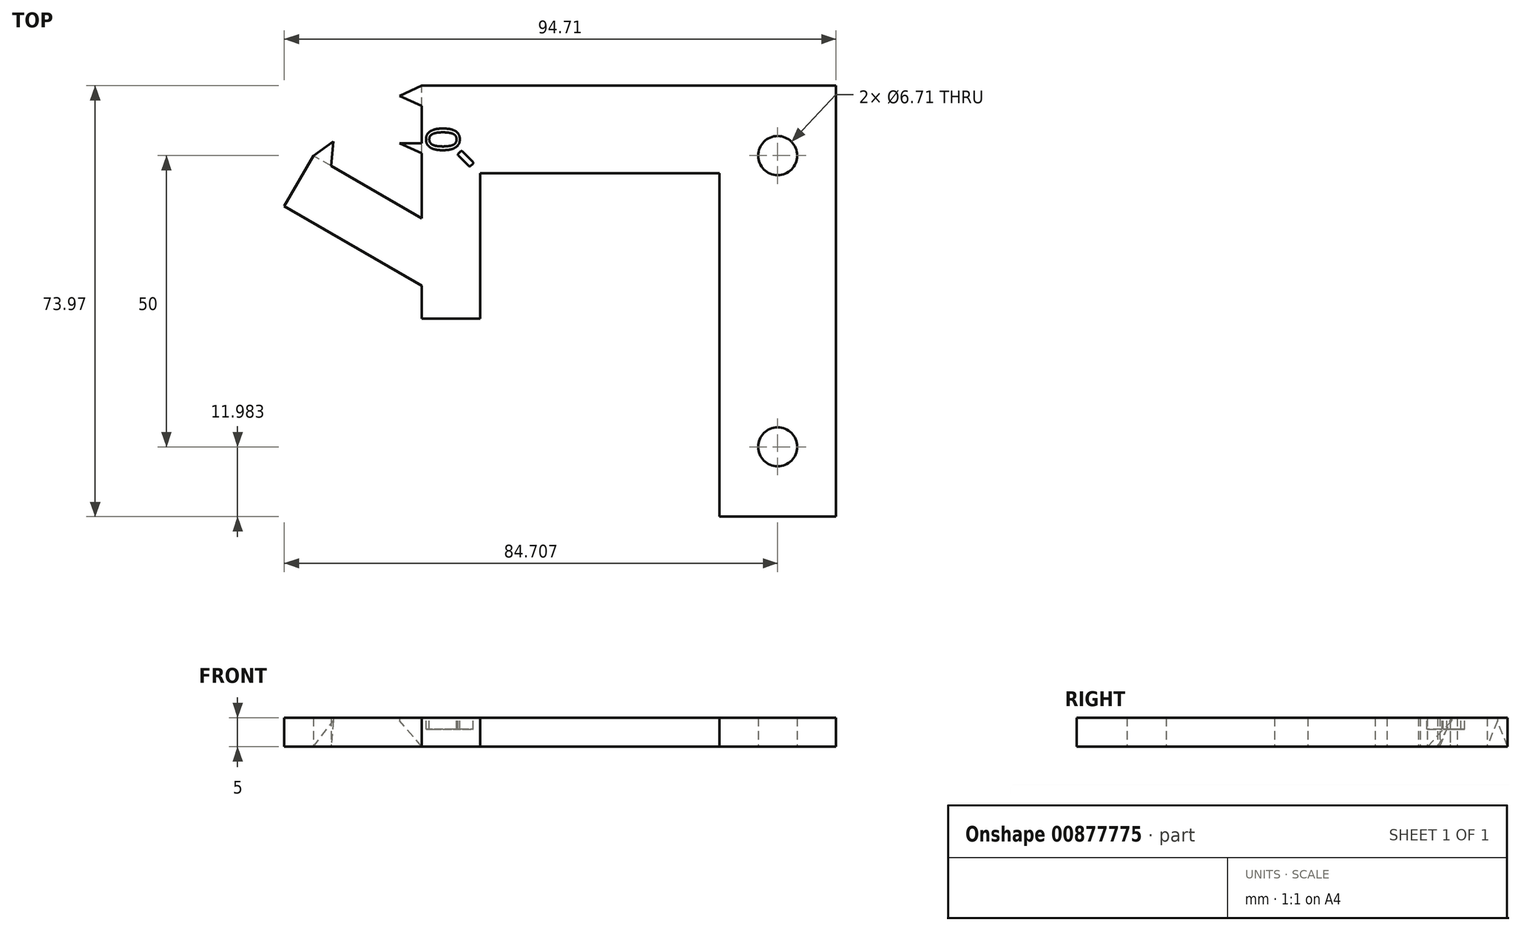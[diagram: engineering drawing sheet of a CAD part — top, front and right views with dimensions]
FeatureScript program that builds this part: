
annotation { "Feature Type Name" : "Feature", "Feature Type Description" : "" }
export const myFeature = defineFeature(function(context is Context, id is Id, definition is map)
    precondition{}
    {
        {
            var Q0;
            Q0=qCreatedBy(makeId("Top.planeOp"),FACE);
            var sketch = newSketch(context, id + "F0", { "sketchPlane" : qUnion([Q0])});
            skLineSegment(sketch, "E0.bottom", {"start": v(11.28, 11.46) * mm, "end": v(21.28, 11.46) * mm});
            skLineSegment(sketch, "E0.top", {"start": v(11.28, 51.46) * mm, "end": v(21.28, 51.46) * mm});
            skLineSegment(sketch, "E0.left", {"start": v(11.28, 11.46) * mm, "end": v(11.28, 51.46) * mm});
            skLineSegment(sketch, "E0.right", {"start": v(21.28, 11.46) * mm, "end": v(21.28, 51.46) * mm});
            skPoint(sketch, "E1.0.midPoint", {"position": v(11.28, 51.46) * mm});
            skLineSegment(sketch, "E2", {"start": v(11.28, 51.46) * mm, "end": v(7.47, 49.71) * mm});
            skLineSegment(sketch, "E3", {"start": v(7.47, 49.71) * mm, "end": v(11.28, 47.97) * mm});
            skLineSegment(sketch, "E4", {"start": v(7.47, 49.71) * mm, "end": v(11.28, 49.71) * mm});
            skLineSegment(sketch, "E5", {"start": v(11.28, 39.84) * mm, "end": v(7.47, 41.58) * mm});
            skLineSegment(sketch, "E6", {"start": v(7.47, 41.58) * mm, "end": v(11.28, 41.58) * mm});
            skLineSegment(sketch, "E7", {"start": v(11.28, 41.58) * mm, "end": v(7.47, 41.58) * mm});
            skLineSegment(sketch, "E8", {"start": v(7.47, 41.58) * mm, "end": v(11.28, 43.33) * mm});
            skLineSegment(sketch, "E9.bottom", {"start": v(-7.32, 39.44) * mm, "end": v(21.28, 22.93) * mm});
            skLineSegment(sketch, "E9.top", {"start": v(-12.32, 30.78) * mm, "end": v(16.28, 14.27) * mm});
            skLineSegment(sketch, "E9.left", {"start": v(-7.32, 39.44) * mm, "end": v(-12.32, 30.78) * mm});
            skLineSegment(sketch, "E9.right", {"start": v(21.28, 22.93) * mm, "end": v(16.28, 14.27) * mm});
            skLineSegment(sketch, "E10", {"start": v(-4.3, 37.7) * mm, "end": v(-3.9, 41.87) * mm});
            skLineSegment(sketch, "E11", {"start": v(-3.9, 41.87) * mm, "end": v(-7.32, 39.44) * mm});
            skLineSegment(sketch, "E12", {"start": v(-3.9, 41.87) * mm, "end": v(-5.81, 38.57) * mm});
            skLineSegment(sketch, "E13.bottom", {"start": v(62.39, -22.51) * mm, "end": v(82.39, -22.51) * mm});
            skLineSegment(sketch, "E13.top", {"start": v(62.39, 51.46) * mm, "end": v(82.39, 51.46) * mm});
            skLineSegment(sketch, "E13.left", {"start": v(62.39, -22.51) * mm, "end": v(62.39, 51.46) * mm});
            skLineSegment(sketch, "E13.right", {"start": v(82.39, -22.51) * mm, "end": v(82.39, 51.46) * mm});
            skCircle(sketch, "E14", {"center": v(72.39, -10.53) * mm, "radius": 3.35 * mm});
            skCircle(sketch, "E15", {"center": v(72.39, 39.47) * mm, "radius": 3.35 * mm});
            skLineSegment(sketch, "E16", {"start": v(72.39, 39.47) * mm, "end": v(72.39, -10.53) * mm});
            skLineSegment(sketch, "E17", {"start": v(72.39, -10.53) * mm, "end": v(72.39, -22.51) * mm});
            skLineSegment(sketch, "E18", {"start": v(72.39, 39.47) * mm, "end": v(72.39, 51.46) * mm});
            skLineSegment(sketch, "E19.bottom", {"start": v(62.39, 51.46) * mm, "end": v(21.28, 51.46) * mm});
            skLineSegment(sketch, "E19.top", {"start": v(62.39, 36.46) * mm, "end": v(21.28, 36.46) * mm});
            skLineSegment(sketch, "E19.left", {"start": v(62.39, 51.46) * mm, "end": v(62.39, 36.46) * mm});
            skLineSegment(sketch, "E19.right", {"start": v(21.28, 51.46) * mm, "end": v(21.28, 36.46) * mm});
            skLineSegment(sketch, "E20", {"start": v(62.39, 36.46) * mm, "end": v(62.39, 51.46) * mm});
            skLineSegment(sketch, "E21", {"start": v(21.28, 36.46) * mm, "end": v(21.28, 51.46) * mm});
            skSolve(sketch);
        }
        {
            var Q0;
            {var subQ6=sQuery(id+"F0.wireOp",EDGE,"47bd21e5-315e-477f-9ace-8077bcce72af.top");Q0=makeQuery(id+"F0.imprint","IMPRINT",FACE,{"disambiguationData":[TD([[makeQuery(id+"F0.imprint","IMPRINT",EDGE,{"derivedFrom":subQ6}),1.0]])]});}
            var Q1;
            {var subQ11=sQuery(id+"F0.wireOp",EDGE,"47bd21e5-315e-477f-9ace-8077bcce72af.bottom");Q1=makeQuery(id+"F0.imprint","IMPRINT",FACE,{"disambiguationData":[TD([[makeQuery(id+"F0.imprint","IMPRINT",EDGE,{"derivedFrom":subQ11}),-1.0]])]});}
            var Q2;
            {var subQ4=sQuery(id+"F0.wireOp",EDGE,"E0.bottom");Q2=makeQuery(id+"F0.imprint","IMPRINT",FACE,{"disambiguationData":[TD([[makeQuery(id+"F0.imprint","IMPRINT",EDGE,{"derivedFrom":subQ4}),1.0]])]});}
            var Q3;
            {var subQ5=sQuery(id+"F0.wireOp",EDGE,"E9.left");Q3=makeQuery(id+"F0.imprint","IMPRINT",FACE,{"disambiguationData":[TD([[makeQuery(id+"F0.imprint","IMPRINT",EDGE,{"derivedFrom":subQ5}),1.0]])]});}
            var Q4;
            {var subQ5=sQuery(id+"F0.wireOp",EDGE,"E9.right");Q4=makeQuery(id+"F0.imprint","IMPRINT",FACE,{"disambiguationData":[TD([[makeQuery(id+"F0.imprint","IMPRINT",EDGE,{"derivedFrom":subQ5}),-1.0]])]});}
            var Q5;
            {var subQ6=sQuery(id+"F0.wireOp",EDGE,"E0.top");Q5=makeQuery(id+"F0.imprint","IMPRINT",FACE,{"disambiguationData":[TD([[makeQuery(id+"F0.imprint","IMPRINT",EDGE,{"derivedFrom":subQ6}),-1.0]])]});}
            var Q6;
            {var subQ0=sQuery(id+"F0.wireOp",EDGE,"E5");Q6=makeQuery(id+"F0.imprint","IMPRINT",FACE,{"disambiguationData":[TD([[makeQuery(id+"F0.imprint","IMPRINT",EDGE,{"derivedFrom":subQ0}),-1.0]])]});}
            var Q7;
            {var subQ0=sQuery(id+"F0.wireOp",EDGE,"E7");Q7=makeQuery(id+"F0.imprint","IMPRINT",FACE,{"disambiguationData":[TD([[makeQuery(id+"F0.imprint","IMPRINT",EDGE,{"derivedFrom":subQ0}),-1.0]])]});}
            var Q8;
            {var subQ0=sQuery(id+"F0.wireOp",EDGE,"E3");Q8=makeQuery(id+"F0.imprint","IMPRINT",FACE,{"disambiguationData":[TD([[makeQuery(id+"F0.imprint","IMPRINT",EDGE,{"derivedFrom":subQ0}),1.0]])]});}
            var Q9;
            {var subQ0=sQuery(id+"F0.wireOp",EDGE,"E2");Q9=makeQuery(id+"F0.imprint","IMPRINT",FACE,{"disambiguationData":[TD([[makeQuery(id+"F0.imprint","IMPRINT",EDGE,{"derivedFrom":subQ0}),1.0]])]});}
            var Q10;
            {var subQ0=sQuery(id+"F0.wireOp",EDGE,"E10");Q10=makeQuery(id+"F0.imprint","IMPRINT",FACE,{"disambiguationData":[TD([[makeQuery(id+"F0.imprint","IMPRINT",EDGE,{"derivedFrom":subQ0}),1.0]])]});}
            var Q11;
            {var subQ0=sQuery(id+"F0.wireOp",EDGE,"E11");Q11=makeQuery(id+"F0.imprint","IMPRINT",FACE,{"disambiguationData":[TD([[makeQuery(id+"F0.imprint","IMPRINT",EDGE,{"derivedFrom":subQ0}),1.0]])]});}
            var Q12;
            Q12=makeQuery(id+"F0.imprint","IMPRINT",FACE,{"disambiguationData":[TD([[makeQuery(id+"F0.imprint","IMPRINT",EDGE,{"derivedFrom":sQuery(id+"F0.wireOp",EDGE,"E19.bottom")}),1.0]])]});
            var Q13;
            {var subQ5=sQuery(id+"F0.wireOp",EDGE,"E13.left");Q13=makeQuery(id+"F0.imprint","IMPRINT",FACE,{"disambiguationData":[TD([[makeQuery(id+"F0.imprint","IMPRINT",EDGE,{"derivedFrom":subQ5}),-1.0]])]});}
            var Q14;
            {var subQ5=sQuery(id+"F0.wireOp",EDGE,"E13.right");Q14=makeQuery(id+"F0.imprint","IMPRINT",FACE,{"disambiguationData":[TD([[makeQuery(id+"F0.imprint","IMPRINT",EDGE,{"derivedFrom":subQ5}),1.0]])]});}
            extrude(context, id + "F1", {"entities" : qUnion([Q0, Q1, Q2, Q3, Q4, Q5, Q6, Q7, Q8, Q9, Q10, Q11, Q12, Q13, Q14]), "depth" : 5 * mm, "offsetDistance" : 25 * mm});
        }
        {
            var Q0;
            Q0=makeQuery(id+"F1.opExtrude","CAP_FACE",FACE,{"disambiguationData":[OSD([sQuery(id+"F0.wireOp",EDGE,"E0.bottom"),sQuery(id+"F0.wireOp",EDGE,"E0.top"),sQuery(id+"F0.wireOp",EDGE,"E0.left"),sQuery(id+"F0.wireOp",EDGE,"E0.right"),sQuery(id+"F0.wireOp",EDGE,"E2"),sQuery(id+"F0.wireOp",EDGE,"E3"),sQuery(id+"F0.wireOp",EDGE,"E5"),sQuery(id+"F0.wireOp",EDGE,"E8"),sQuery(id+"F0.wireOp",EDGE,"E9.bottom"),sQuery(id+"F0.wireOp",EDGE,"E9.top"),sQuery(id+"F0.wireOp",EDGE,"E9.left"),sQuery(id+"F0.wireOp",EDGE,"E10"),sQuery(id+"F0.wireOp",EDGE,"E11"),sQuery(id+"F0.wireOp",EDGE,"E13.bottom"),sQuery(id+"F0.wireOp",EDGE,"E13.top"),sQuery(id+"F0.wireOp",EDGE,"E13.left"),sQuery(id+"F0.wireOp",EDGE,"E13.right"),sQuery(id+"F0.wireOp",EDGE,"E14"),sQuery(id+"F0.wireOp",EDGE,"E15"),sQuery(id+"F0.wireOp",EDGE,"E19.bottom"),sQuery(id+"F0.wireOp",EDGE,"E19.top")])],"isStart":false});
            var sketch = newSketch(context, id + "F2", { "sketchPlane" : qUnion([Q0])});
            skText(sketch, "E22", { "text": "0\n", "fontName": "OpenSans-Regular.ttf"});
            skLineSegment(sketch, "E23", {"start": v(18.27, 40.17) * mm, "end": v(20.04, 38.4) * mm});
            skLineSegment(sketch, "E24", {"start": v(20.04, 38.05) * mm, "end": v(19.69, 37.7) * mm});
            skLineSegment(sketch, "E25", {"start": v(19.34, 37.7) * mm, "end": v(17.57, 39.46) * mm});
            skLineSegment(sketch, "E26", {"start": v(17.57, 39.82) * mm, "end": v(17.92, 40.17) * mm});
            skPoint(sketch, "E27.visualSharp", {"position": v(20.22, 38.23) * mm});
            skArc(sketch, "E27.filletArc", {"start": v(20.04, 38.05) * mm, "mid": v(20.12, 38.23) * mm, "end": v(20.04, 38.4) * mm});
            skPoint(sketch, "E28.visualSharp", {"position": v(19.51, 37.52) * mm});
            skArc(sketch, "E28.filletArc", {"start": v(19.34, 37.7) * mm, "mid": v(19.51, 37.62) * mm, "end": v(19.69, 37.7) * mm});
            skArc(sketch, "E29.filletArc", {"start": v(17.57, 39.82) * mm, "mid": v(17.5, 39.64) * mm, "end": v(17.57, 39.46) * mm});
            skPoint(sketch, "E30.visualSharp", {"position": v(18.1, 40.35) * mm});
            skArc(sketch, "E30.filletArc", {"start": v(18.27, 40.17) * mm, "mid": v(18.1, 40.25) * mm, "end": v(17.92, 40.17) * mm});
            skLineSegment(sketch, "E31", {"start": v(21.28, 36.46) * mm, "end": v(19.87, 37.87) * mm, "construction": true});
            const initialGuessF2  = {"E22": [0.01774, 0.04, 0, 1, 0.00568]};
            skSetInitialGuess(sketch, initialGuessF2);
            skSolve(sketch);
        }
        {
            var Q0;
            Q0 = qSketchRegion(id + "F2", true);
            extrude(context, id + "F3", {"entities" : qUnion([Q0]), "operationType" : NewBodyOperationType.REMOVE, "oppositeDirection" : true, "depth" : 2 * mm, "offsetDistance" : 25 * mm});
        }
        {
            var Q0;
            Q0=makeQuery(id+"F1.opExtrude","SWEPT_FACE",FACE,{"disambiguationData":[OSD([sQuery(id+"F0.wireOp",EDGE,"E0.top"),sQuery(id+"F0.wireOp",EDGE,"E13.top"),sQuery(id+"F0.wireOp",EDGE,"E19.bottom")])]});
            var sketch = newSketch(context, id + "F4", { "sketchPlane" : qUnion([Q0])});
            skLineSegment(sketch, "E32", {"start": v(-11.28, 0) * mm, "end": v(-7.47, 0) * mm});
            skLineSegment(sketch, "E33", {"start": v(-7.47, 0) * mm, "end": v(-7.47, 4.5) * mm});
            skLineSegment(sketch, "E34", {"start": v(-7.47, 4.5) * mm, "end": v(-11.28, 0) * mm});
            skSolve(sketch);
        }
        {
            var Q0;
            Q0 = qSketchRegion(id + "F4", true);
            var Q1;
            Q1=makeQuery(id+"F1.opExtrude","SWEPT_FACE",FACE,{"disambiguationData":[OSD([sQuery(id+"F0.wireOp",EDGE,"E9.bottom")])]});
            extrude(context, id + "F5", {"entities" : qUnion([Q0]), "operationType" : NewBodyOperationType.REMOVE, "endBound" : BoundingType.UP_TO_SURFACE, "oppositeDirection" : true, "depth" : 25 * mm, "endBoundEntityFace" : qUnion([Q1]), "offsetDistance" : 25 * mm});
        }
        {
            var Q0;
            Q0=makeQuery(id+"F1.opExtrude","SWEPT_FACE",FACE,{"disambiguationData":[OSD([sQuery(id+"F0.wireOp",EDGE,"E9.left")])]});
            var sketch = newSketch(context, id + "F6", { "sketchPlane" : qUnion([Q0])});
            skLineSegment(sketch, "E35", {"start": v(-30.5, 0) * mm, "end": v(-34.3, 0) * mm});
            skLineSegment(sketch, "E36", {"start": v(-34.3, 0) * mm, "end": v(-34.3, 4.5) * mm});
            skLineSegment(sketch, "E37", {"start": v(-34.3, 4.5) * mm, "end": v(-30.5, 0) * mm});
            skSolve(sketch);
        }
        {
            var Q0;
            Q0 = qSketchRegion(id + "F6", true);
            var Q1;
            {var subQ0=sQuery(id+"F0.wireOp",EDGE,"E0.left");Q1=makeQuery(id+"F1.opExtrude","SWEPT_FACE",FACE,{"disambiguationData":[OSD([subQ0]),TDD([makeQuery(id+"F0.imprint","IMPRINT",EDGE,{"disambiguationData":[TD([[makeQuery(id+"F0.imprint","INTERSECT",VERTEX,{"derivedFrom":[subQ0,sQuery(id+"F0.wireOp",EDGE,"E5")]}),1.0]])],"derivedFrom":subQ0})])]});}
            extrude(context, id + "F7", {"entities" : qUnion([Q0]), "operationType" : NewBodyOperationType.REMOVE, "endBound" : BoundingType.UP_TO_SURFACE, "oppositeDirection" : true, "depth" : 25 * mm, "endBoundEntityFace" : qUnion([Q1]), "offsetDistance" : 25 * mm});
        }
    });
